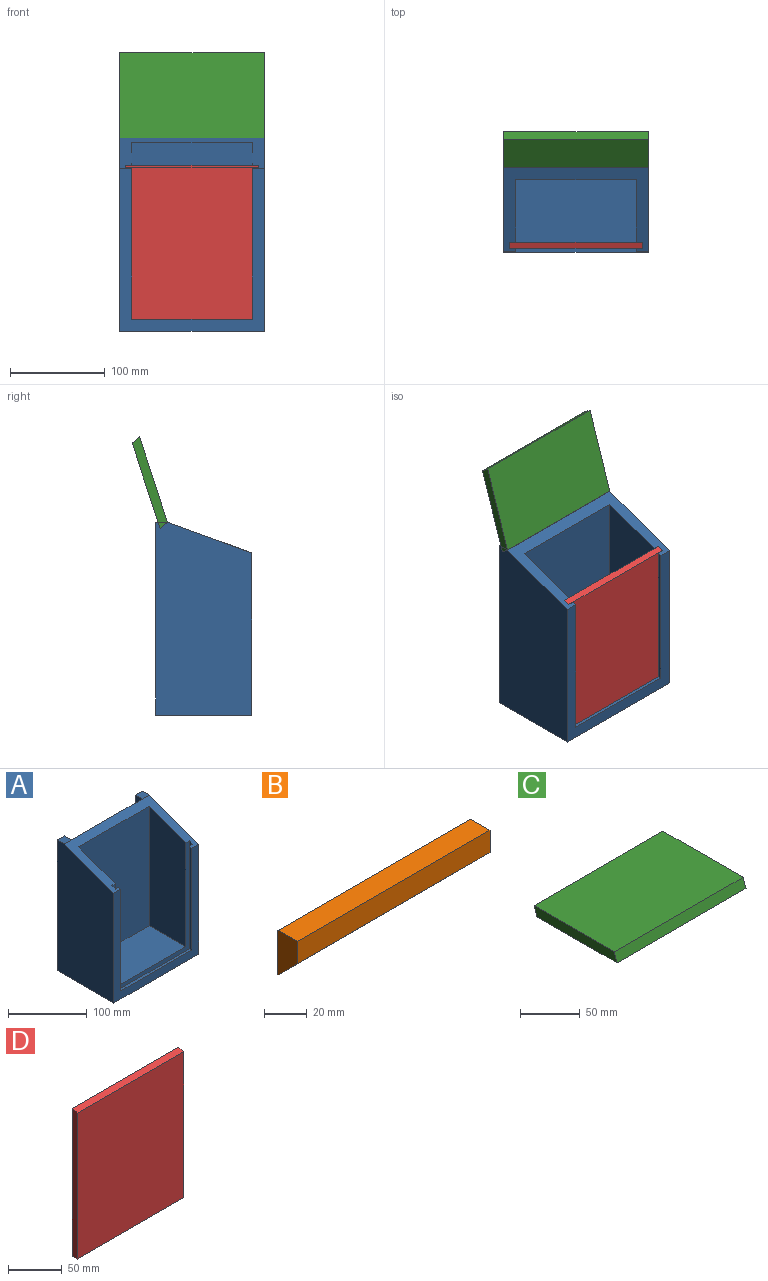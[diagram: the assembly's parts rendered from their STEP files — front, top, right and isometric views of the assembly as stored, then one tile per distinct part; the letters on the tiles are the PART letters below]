
ASSEMBLY  parts=4 mates=3
PART A: 24 faces, bbox 152.4x101.6x203.2 mm
  f0: plane 152.4x88.9mm, normal (0,-0.34,0.94), area 4033.6mm2, adj f2,f3,f4,f5,f7,f8,f10,f11
  f1: plane 127x3.94mm, normal (0,0,1), area 499.9mm2, adj f2,f3,f4,f14
  f2: plane 159.58x3.94mm, normal (-1,0,0), area 625.3mm2, adj f0,f1,f4,f14
  f3: plane 159.58x3.94mm, normal (1,0,0), area 625.3mm2, adj f0,f1,f4,f14
  f4: plane 170.84x152.4mm, normal (0,-1,0), area 5952.3mm2, adj f0,f1,f2,f3,f5,f6,f7
  f5: plane 203.2x101.6mm, normal (-1,0,0), area 19206.9mm2, adj f0,f4,f6,f20,f23
  f6: plane 152.4x101.6mm, normal (0,0,-1), area 15483.8mm2, adj f4,f5,f7,f23
  f7: plane 203.2x101.6mm, normal (1,0,0), area 19206.9mm2, adj f0,f4,f6,f19,f23
  f8: plane 190.5x127mm, normal (0,1,0), area 24193.5mm2, adj f0,f18,f21,f22
  f9: plane 127x65.91mm, normal (0,0,1), area 8371mm2, adj f10,f11,f12,f16
  f10: plane 185.88x127mm, normal (0,-1,0), area 23606.5mm2, adj f0,f9,f11,f12
  f11: plane 185.88x65.91mm, normal (-1,0,0), area 11461.2mm2, adj f0,f9,f10,f16
  f12: plane 185.88x65.91mm, normal (1,0,0), area 11461.2mm2, adj f0,f9,f10,f16
  f13: plane 168.24x6.35mm, normal (1,0,0), area 1061mm2, adj f0,f14,f16,f17
  f14: plane 165.93x139.7mm, normal (0,1,0), area 2913.7mm2, adj f0,f1,f2,f3,f13,f15,f17
  f15: plane 168.24x6.35mm, normal (-1,0,0), area 1061mm2, adj f0,f14,f16,f17
  f16: plane 168.24x139.7mm, normal (0,-1,0), area 2943.1mm2, adj f0,f9,f11,f12,f13,f15,f17
  f17: plane 139.7x6.35mm, normal (0,0,1), area 887.1mm2, adj f13,f14,f15,f16
  f18: plane 190.5x12.7mm, normal (-1,0,0), area 2419.3mm2, adj f8,f19,f22,f23
  f19: plane 12.7x12.7mm, normal (0,0,1), area 161.3mm2, adj f0,f7,f18,f23
  f20: plane 12.7x12.7mm, normal (0,0,1), area 161.3mm2, adj f0,f5,f21,f23
  f21: plane 190.5x12.7mm, normal (1,0,0), area 2419.3mm2, adj f8,f20,f22,f23
  f22: plane 127x12.7mm, normal (0,0,1), area 1612.9mm2, adj f8,f18,f21,f23
  f23: plane 203.2x152.4mm, normal (0,1,0), area 6774.2mm2, adj f5,f6,f7,f18,f19,f20,f21,f22
PART B: 6 faces, bbox 127x12.7x25.4 mm
  f0: plane 127x12.7mm, normal (0,-1,0), area 1612.9mm2, adj f1,f3,f4,f5
  f1: plane 127x12.7mm, normal (0,-0.71,-0.71), area 2281mm2, adj f0,f2,f4,f5
  f2: plane 127x25.4mm, normal (0,1,0), area 3225.8mm2, adj f1,f3,f4,f5
  f3: plane 127x12.7mm, normal (0,0,1), area 1612.9mm2, adj f0,f2,f4,f5
  f4: plane 25.4x12.7mm, normal (1,0,0), area 241.9mm2, adj f0,f1,f2,f3
  f5: plane 25.4x12.7mm, normal (-1,0,0), area 241.9mm2, adj f0,f1,f2,f3
PART C: 6 faces, bbox 152.4x98.1x9.5 mm
  f0: plane 152.4x94.62mm, normal (0,0,1), area 14419.3mm2, adj f2,f3,f4,f5
  f1: plane 152.4x94.62mm, normal (0,0,-1), area 14419.3mm2, adj f2,f3,f4,f5
  f2: plane 98.08x9.53mm, normal (-1,0,0), area 901.2mm2, adj f0,f1,f4,f5
  f3: plane 98.08x9.53mm, normal (1,0,0), area 901.2mm2, adj f0,f1,f4,f5
  f4: plane 152.4x9.53mm, normal (0,0.94,-0.34), area 1544.8mm2, adj f0,f1,f2,f3
  f5: plane 152.4x9.53mm, normal (0,-0.94,0.34), area 1544.8mm2, adj f0,f1,f2,f3
PART D: 6 faces, bbox 139.7x6.4x168.2 mm
  f0: plane 165.94x139.7mm, normal (0,-1,0), area 23181.6mm2, adj f1,f3,f4,f5
  f1: plane 139.7x6.35mm, normal (0,0,-1), area 887.1mm2, adj f0,f2,f4,f5
  f2: plane 168.25x139.7mm, normal (0,1,0), area 23504.5mm2, adj f1,f3,f4,f5
  f3: plane 139.7x6.35mm, normal (0,-0.34,0.94), area 944mm2, adj f0,f2,f4,f5
  f4: plane 168.25x6.35mm, normal (1,0,0), area 1061mm2, adj f0,f1,f2,f3
  f5: plane 168.25x6.35mm, normal (-1,0,0), area 1061mm2, adj f0,f1,f2,f3
PLACE A t=(-7.4,80.14,-41.66)mm fixed
PLACE B t=(-7.4,80.14,104.39)mm
PLACE C rot(axis=(-1,0,0),108.1deg) t=(-11.5,94.89,206.52)mm
PLACE D t=(-7.4,-4.82,-35.31)mm
MATE fastened A.f8 <-> B.f0  axis (0,1,0) through (-7.4,80.14,66.29)mm
MATE planar A.f7 <-> C.f3  axis (1,0,0) through (68.8,43.63,53.14)mm
MATE fastened D.f1 <-> A.f17  axis (0,0,-1) through (-7.4,-1.65,-35.31)mm
